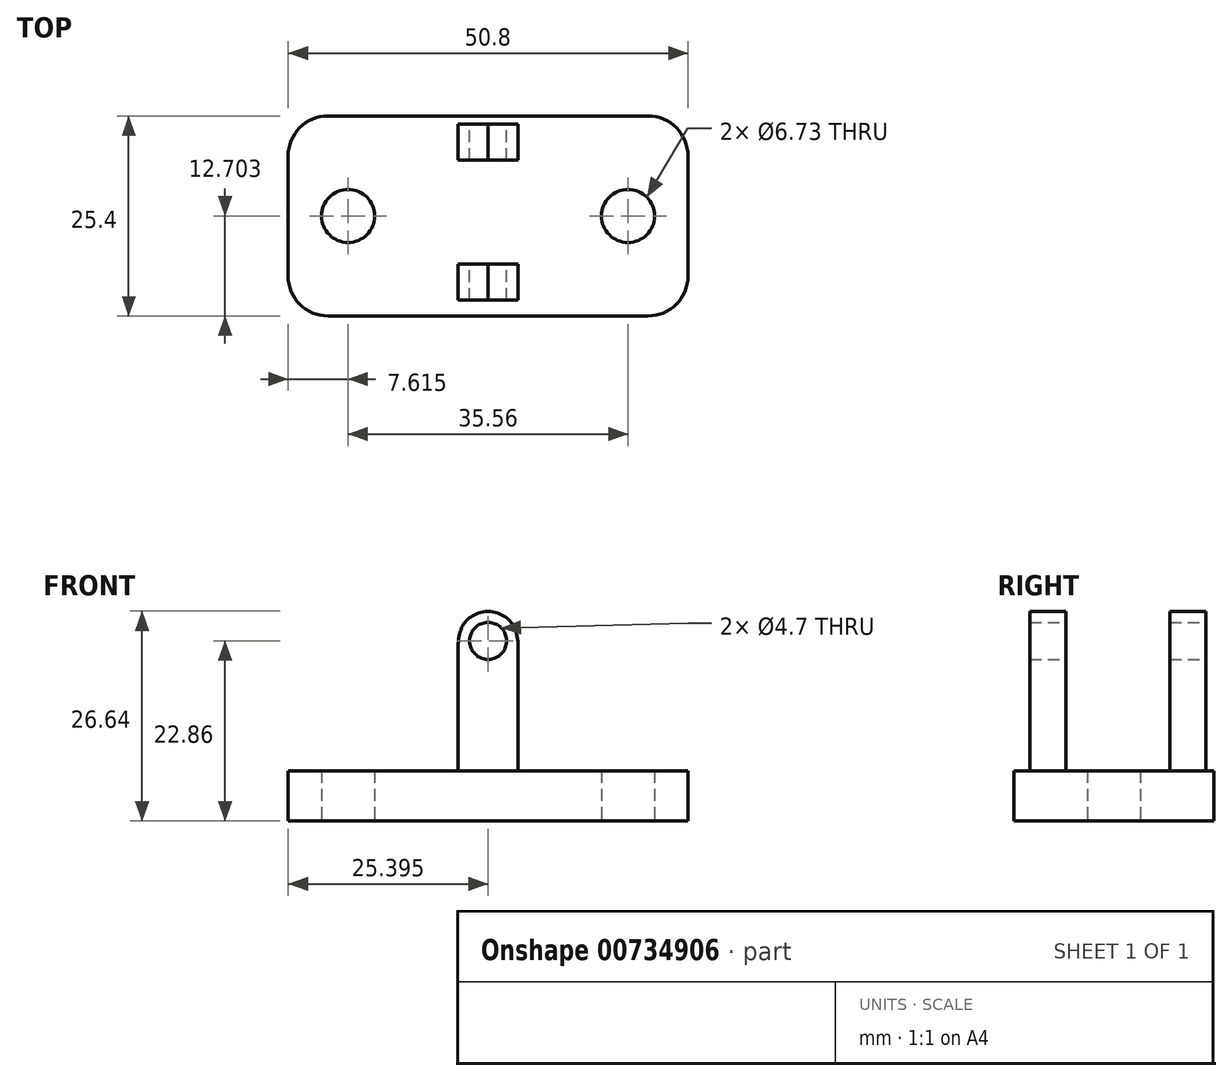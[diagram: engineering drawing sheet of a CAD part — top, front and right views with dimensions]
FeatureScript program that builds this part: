
annotation { "Feature Type Name" : "Feature", "Feature Type Description" : "" }
export const myFeature = defineFeature(function(context is Context, id is Id, definition is map)
    precondition{}
    {
        {
            var Q0;
            Q0=qCreatedBy(makeId("Top.planeOp"),FACE);
            var sketch = newSketch(context, id + "F0", { "sketchPlane" : qUnion([Q0])});
            skLineSegment(sketch, "E0.bottom", {"start": v(-10.8, 14.36) * mm, "end": v(40, 14.36) * mm});
            skLineSegment(sketch, "E0.top", {"start": v(-10.8, -11.04) * mm, "end": v(40, -11.04) * mm});
            skLineSegment(sketch, "E0.left", {"start": v(-10.8, 14.36) * mm, "end": v(-10.8, -11.04) * mm});
            skLineSegment(sketch, "E0.right", {"start": v(40, 14.36) * mm, "end": v(40, -11.04) * mm});
            skCircle(sketch, "E1", {"center": v(-3.17, 1.66) * mm, "radius": 3.37 * mm});
            skCircle(sketch, "E2", {"center": v(32.39, 1.66) * mm, "radius": 3.37 * mm});
            skSolve(sketch);
        }
        {
            var Q0;
            Q0=qSketchRegion(id+"F0",true);
            extrude(context, id + "F1", {"entities" : qUnion([Q0]), "depth" : 6.35 * mm, "offsetDistance" : 25.4 * mm});
        }
        {
            var Q0;
            Q0=makeQuery(id+"F1.opExtrude","SWEPT_EDGE",EDGE,{"disambiguationData":[OSD([sQuery(id+"F0.wireOp",EDGE,"E0.top"),sQuery(id+"F0.wireOp",EDGE,"E0.right")])]});
            var Q1;
            Q1=makeQuery(id+"F1.opExtrude","SWEPT_EDGE",EDGE,{"disambiguationData":[OSD([sQuery(id+"F0.wireOp",EDGE,"E0.bottom"),sQuery(id+"F0.wireOp",EDGE,"E0.right")])]});
            var Q2;
            Q2=makeQuery(id+"F1.opExtrude","SWEPT_EDGE",EDGE,{"disambiguationData":[OSD([sQuery(id+"F0.wireOp",EDGE,"E0.top"),sQuery(id+"F0.wireOp",EDGE,"E0.left")])]});
            var Q3;
            Q3=makeQuery(id+"F1.opExtrude","SWEPT_EDGE",EDGE,{"disambiguationData":[OSD([sQuery(id+"F0.wireOp",EDGE,"E0.bottom"),sQuery(id+"F0.wireOp",EDGE,"E0.left")])]});
            fillet(context, id + "F2", {"entities" : qUnion([Q0, Q1, Q2, Q3]), "radius" : 5.08 * mm, "tangentPropagation" : true, "allowEdgeOverflow" : false});
        }
        {
            var Q0;
            Q0=makeQuery(id+"F1.opExtrude","CAP_FACE",FACE,{"disambiguationData":[OSD([sQuery(id+"F0.wireOp",EDGE,"E0.bottom"),sQuery(id+"F0.wireOp",EDGE,"E0.top"),sQuery(id+"F0.wireOp",EDGE,"E0.left"),sQuery(id+"F0.wireOp",EDGE,"E0.right"),sQuery(id+"F0.wireOp",EDGE,"E1"),sQuery(id+"F0.wireOp",EDGE,"E2")])],"isStart":false});
            var sketch = newSketch(context, id + "F3", { "sketchPlane" : qUnion([Q0])});
            skLineSegment(sketch, "E3.bottom", {"start": v(10.8, 13.35) * mm, "end": v(18.42, 13.35) * mm});
            skLineSegment(sketch, "E3.top", {"start": v(10.8, 8.78) * mm, "end": v(18.42, 8.78) * mm});
            skLineSegment(sketch, "E3.left", {"start": v(10.8, 13.35) * mm, "end": v(10.8, 8.78) * mm});
            skLineSegment(sketch, "E3.right", {"start": v(18.42, 13.35) * mm, "end": v(18.42, 8.78) * mm});
            skPoint(sketch, "E4.oppositeSnap0", {"position": v(18.8, -9) * mm});
            skLineSegment(sketch, "E4.bottom", {"start": v(10.8, -4.43) * mm, "end": v(18.42, -4.43) * mm});
            skLineSegment(sketch, "E4.top", {"start": v(10.8, -9) * mm, "end": v(18.42, -9) * mm});
            skLineSegment(sketch, "E4.left", {"start": v(10.8, -4.43) * mm, "end": v(10.8, -9) * mm});
            skLineSegment(sketch, "E4.right", {"start": v(18.42, -4.43) * mm, "end": v(18.42, -9) * mm});
            skSolve(sketch);
        }
        {
            var Q0;
            Q0=qSketchRegion(id+"F3",true);
            extrude(context, id + "F4", {"entities" : qUnion([Q0]), "operationType" : NewBodyOperationType.ADD, "depth" : 20.32 * mm, "offsetDistance" : 25.4 * mm});
        }
        {
            var Q0;
            Q0=makeQuery(id+"F4.opExtrude","SWEPT_FACE",FACE,{"disambiguationData":[OSD([sQuery(id+"F3.wireOp",EDGE,"E3.bottom")])]});
            var sketch = newSketch(context, id + "F5", { "sketchPlane" : qUnion([Q0])});
            skCircle(sketch, "E5", {"center": v(-14.6, 22.86) * mm, "radius": 2.35 * mm});
            skPoint(sketch, "E5.centerSnap0", {"position": v(-14.6, 26.67) * mm});
            skSolve(sketch);
        }
        {
            var Q0;
            Q0 = qSketchRegion(id + "F5", true);
            extrude(context, id + "F6", {"entities" : qUnion([Q0]), "operationType" : NewBodyOperationType.REMOVE, "oppositeDirection" : true, "depth" : 25.4 * mm, "offsetDistance" : 25.4 * mm});
        }
        {
            var Q0;
            Q0=makeQuery(id+"F4.opExtrude","CAP_EDGE",EDGE,{"disambiguationData":[OSD([sQuery(id+"F3.wireOp",EDGE,"E4.right")])],"isStart":false});
            var Q1;
            Q1=makeQuery(id+"F4.opExtrude","CAP_EDGE",EDGE,{"disambiguationData":[OSD([sQuery(id+"F3.wireOp",EDGE,"E4.left")])],"isStart":false});
            var Q2;
            Q2=makeQuery(id+"F4.opExtrude","CAP_EDGE",EDGE,{"disambiguationData":[OSD([sQuery(id+"F3.wireOp",EDGE,"E3.right")])],"isStart":false});
            var Q3;
            Q3=makeQuery(id+"F4.opExtrude","CAP_EDGE",EDGE,{"disambiguationData":[OSD([sQuery(id+"F3.wireOp",EDGE,"E3.left")])],"isStart":false});
            fillet(context, id + "F7", {"entities" : qUnion([Q0, Q1, Q2, Q3]), "radius" : 4.57 * mm, "tangentPropagation" : true, "rho" : 0.5, "crossSection" : FilletCrossSection.CONIC, "allowEdgeOverflow" : false});
        }
    });
